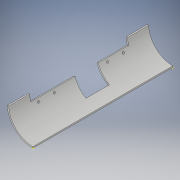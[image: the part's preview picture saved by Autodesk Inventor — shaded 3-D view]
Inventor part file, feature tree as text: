
AUTODESK INVENTOR PART (.ipt)
format: ipt  version: 2017 (Build 210142000, 142)  size: 183,296 bytes
history: native  units: in
note: dims shown in document units (in); Inventor stores cm internally (conversion verified against a paired STEP export)
features: sketch x9, extrude x4, plane x3, hole x1, mirror x1
ambient origin geometry x8: Origin, YZ Plane, XZ Plane, XY Plane, X Axis, Y Axis, Z Axis, Center Point
bodies: Solid1 (feature_tree)
feature tree (18):
  extrude  "Extrusion1"  Depth=2.0472in
  sketch  "Sketch4"  dims[d4=1.4173in d5=1.5354in]
  sketch  "Sketch5"  dims[d6=0.0in d7=0.0in]
  plane  "Work Plane3"
  sketch  "Sketch6"  dims[d9=11.811in d10=0.0in d27=0.0481in]
  sketch  "Sketch7"  dims[d28=2.1654in d30=5.9055in]
  hole  "Hole2"  [1 undecoded]
  extrude  "Extrusion2"  TaperAngle=0.0deg  [1 undecoded]
  plane  "Work Plane4"
  extrude  "Extrusion3"  Depth=11.811in
  extrude  "Extrusion4"  Depth=2.1654in
  plane  "Work Plane5"
  mirror  "Mirror1"
  sketch  "Sketch1"  dims[d0=2.1654in d1=2.0472in]
  sketch  "Sketch8"  dims[d31=2.2441in]
  sketch  "Sketch9"  dims[d32=1.3386in]
  sketch  "Sketch10"  dims[d33=0.2644in]
  sketch  "Sketch11"  dims[d34=0.2644in d35=0.1732in d36=0.2362in d37=0.1575in d38=0.0787in d39=90.0deg d40=0.315in d41=0.8108in d42=5.9055in d43=1.2992in d46=0.5906in d47=1.9685in d48=0.3937in d49=0.0in d50=0.3937in d51=0.0in d52=2.0472in d53=2.1654in d54=15.0deg d55=1.7717in d56=0.0in]
note: 2 required parameter values undecoded (feature->parameter linkage not recoverable at this tier; creation-order binding heuristic only, values carry confidence <= 0.55)
